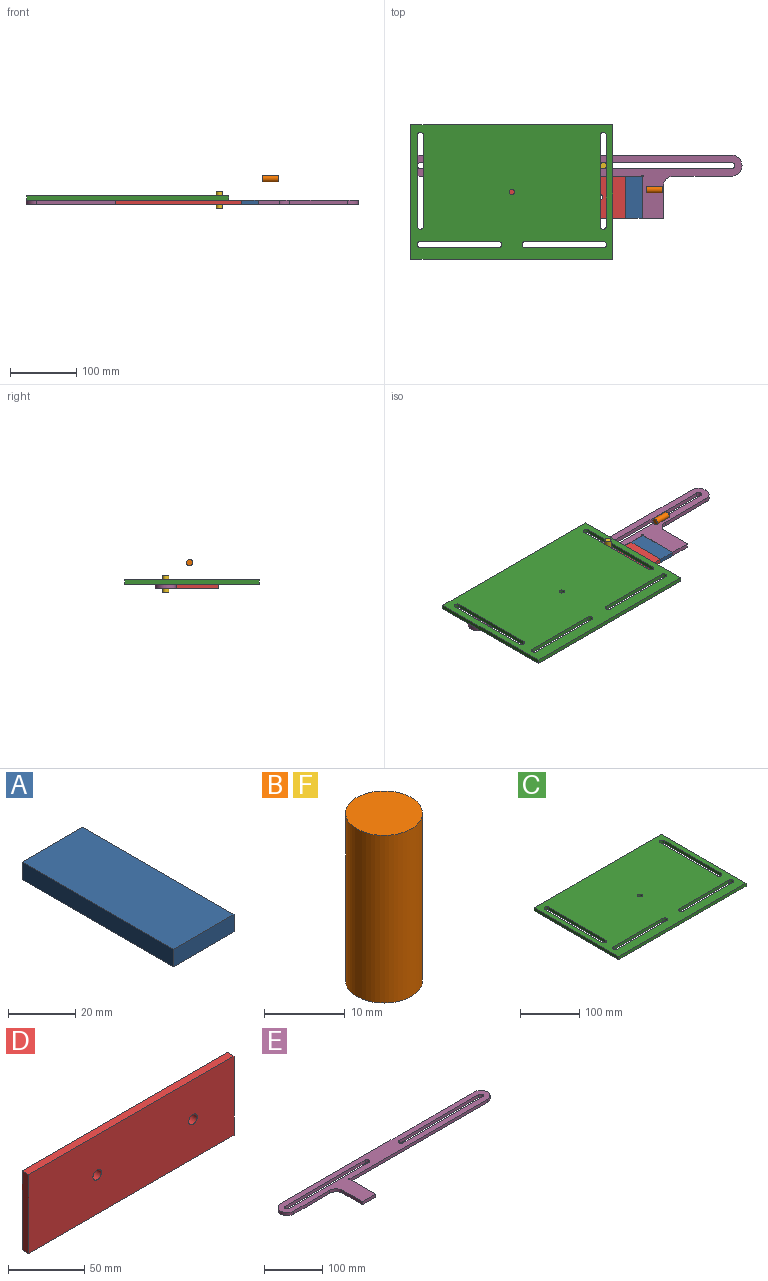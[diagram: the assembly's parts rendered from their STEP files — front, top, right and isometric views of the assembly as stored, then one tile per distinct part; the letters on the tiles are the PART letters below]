
ASSEMBLY  parts=6 mates=6
PART A: 6 faces, bbox 25.4x63.5x6.4 mm
  f0: plane 25.4x6.35mm, normal (0,1,0), area 161.3mm2, adj f1,f3,f4,f5
  f1: plane 63.5x6.35mm, normal (-1,0,0), area 403.2mm2, adj f0,f2,f4,f5
  f2: plane 25.4x6.35mm, normal (0,-1,0), area 161.3mm2, adj f1,f3,f4,f5
  f3: plane 63.5x6.35mm, normal (1,0,0), area 403.2mm2, adj f0,f2,f4,f5
  f4: plane 63.5x25.4mm, normal (0,0,1), area 1612.9mm2, adj f0,f1,f2,f3
  f5: plane 63.5x25.4mm, normal (0,0,-1), area 1612.9mm2, adj f0,f1,f2,f3
PART B: 3 faces, bbox 9.5x9.5x25.4 mm
  f0: cylinder r=4.76mm len=25.4mm, axis (0,0,-1), area 760.1mm2, adj f1,f2
  f1: plane 9.53x9.53mm, normal (0,0,1), area 71.3mm2, adj f0
  f2: plane 9.53x9.53mm, normal (0,0,-1), area 71.3mm2, adj f0
PART C: 23 faces, bbox 304.8x203.2x6.4 mm
  f0: plane 304.8x6.35mm, normal (0,1,0), area 1935.5mm2, adj f1,f20,f21,f22
  f1: plane 203.2x6.35mm, normal (-1,0,0), area 1290.3mm2, adj f0,f2,f21,f22
  f2: plane 304.8x6.35mm, normal (0,-1,0), area 1935.5mm2, adj f1,f20,f21,f22
  f3: cylinder r=4.76mm len=9.53mm, axis (0,0,-1), area 95mm2, adj f4,f16,f21,f22
  f4: plane 136.8x6.35mm, normal (-1,0,0), area 868.7mm2, adj f3,f5,f21,f22
  f5: cylinder r=4.76mm len=9.53mm, axis (0,0,-1), area 95mm2, adj f4,f16,f21,f22
  f6: cylinder r=4.76mm len=9.53mm, axis (0,0,-1), area 95mm2, adj f7,f17,f21,f22
  f7: plane 117.95x6.35mm, normal (0,1,0), area 749mm2, adj f6,f8,f21,f22
  f8: cylinder r=4.76mm len=9.53mm, axis (0,0,-1), area 95mm2, adj f7,f17,f21,f22
  f9: cylinder r=4.76mm len=9.53mm, axis (0,0,-1), area 95mm2, adj f10,f18,f21,f22
  f10: plane 117.95x6.35mm, normal (0,-1,0), area 749mm2, adj f9,f11,f21,f22
  f11: cylinder r=4.76mm len=9.53mm, axis (0,0,-1), area 95mm2, adj f10,f18,f21,f22
  f12: cylinder r=4.76mm len=9.53mm, axis (0,0,-1), area 95mm2, adj f13,f19,f21,f22
  f13: plane 136.8x6.35mm, normal (-1,0,0), area 868.7mm2, adj f12,f14,f21,f22
  f14: cylinder r=4.76mm len=9.53mm, axis (0,0,-1), area 95mm2, adj f13,f19,f21,f22
  f15: cylinder r=3.97mm len=7.94mm, axis (0,0,-1), area 158.3mm2, adj f21,f22
  f16: plane 136.8x6.35mm, normal (1,0,0), area 868.7mm2, adj f3,f5,f21,f22
  f17: plane 117.95x6.35mm, normal (0,-1,0), area 749mm2, adj f6,f8,f21,f22
  f18: plane 117.95x6.35mm, normal (0,1,0), area 749mm2, adj f9,f11,f21,f22
  f19: plane 136.8x6.35mm, normal (1,0,0), area 868.7mm2, adj f12,f14,f21,f22
  f20: plane 203.2x6.35mm, normal (1,0,0), area 1290.3mm2, adj f0,f2,f21,f22
  f21: plane 304.8x203.2mm, normal (0,0,1), area 56747.8mm2, adj f0,f1,f2,f3,f4,f5,f6,f7
  f22: plane 304.8x203.2mm, normal (0,0,-1), area 56747.8mm2, adj f0,f1,f2,f3,f4,f5,f6,f7
PART D: 8 faces, bbox 190.5x6.4x63.5 mm
  f0: plane 63.5x6.35mm, normal (-1,0,0), area 403.2mm2, adj f1,f3,f4,f5
  f1: plane 190.5x6.35mm, normal (0,0,-1), area 1209.7mm2, adj f0,f2,f4,f5
  f2: plane 63.5x6.35mm, normal (1,0,0), area 403.2mm2, adj f1,f3,f4,f5
  f3: plane 190.5x6.35mm, normal (0,0,1), area 1209.7mm2, adj f0,f2,f4,f5
  f4: plane 190.5x63.5mm, normal (0,-1,0), area 11997.8mm2, adj f0,f1,f2,f3,f6,f7
  f5: plane 190.5x63.5mm, normal (0,1,0), area 11997.8mm2, adj f0,f1,f2,f3,f6,f7
  f6: cylinder r=3.97mm len=7.94mm, axis (0,-1,0), area 158.3mm2, adj f4,f5
  f7: cylinder r=3.97mm len=7.94mm, axis (0,-1,0), area 158.3mm2, adj f4,f5
PART E: 20 faces, bbox 501.7x95.3x6.4 mm
  f0: cylinder r=4.76mm len=9.53mm, axis (0,0,-1), area 95mm2, adj f1,f17,f18,f19
  f1: plane 193.68x6.35mm, normal (0,-1,0), area 1229.8mm2, adj f0,f2,f18,f19
  f2: cylinder r=4.76mm len=9.53mm, axis (0,0,-1), area 95mm2, adj f1,f17,f18,f19
  f3: plane 31.75x6.35mm, normal (0,-1,0), area 201.6mm2, adj f4,f15,f18,f19
  f4: plane 61.9x6.35mm, normal (1,0,0), area 393.1mm2, adj f3,f5,f18,f19
  f5: cylinder r=1.6mm len=6.35mm, axis (0,0,-1), area 47.9mm2, adj f4,f6,f18,f19
  f6: plane 333.38x6.35mm, normal (0,-1,0), area 2116.9mm2, adj f5,f7,f18,f19
  f7: cylinder r=15.88mm len=31.75mm, axis (0,0,-1), area 316.7mm2, adj f6,f8,f18,f19
  f8: plane 469.9x6.35mm, normal (0,1,0), area 2983.9mm2, adj f7,f9,f18,f19
  f9: cylinder r=15.88mm len=31.75mm, axis (0,0,-1), area 316.7mm2, adj f8,f10,f18,f19
  f10: plane 87.3x6.35mm, normal (0,-1,0), area 554.4mm2, adj f9,f11,f18,f19
  f11: cylinder r=15.88mm len=15.88mm, axis (0,0,-1), area 158.3mm2, adj f10,f15,f18,f19
  f12: plane 193.68x6.35mm, normal (0,-1,0), area 1229.8mm2, adj f13,f16,f18,f19
  f13: cylinder r=4.76mm len=9.53mm, axis (0,0,-1), area 95mm2, adj f12,f14,f18,f19
  f14: plane 193.68x6.35mm, normal (0,1,0), area 1229.8mm2, adj f13,f16,f18,f19
  f15: plane 47.63x6.35mm, normal (-1,0,0), area 302.4mm2, adj f3,f11,f18,f19
  f16: cylinder r=4.76mm len=9.53mm, axis (0,0,-1), area 95mm2, adj f12,f14,f18,f19
  f17: plane 193.68x6.35mm, normal (0,1,0), area 1229.8mm2, adj f0,f2,f18,f19
  f18: plane 501.65x95.25mm, normal (0,0,1), area 13943.2mm2, adj f0,f1,f2,f3,f4,f5,f6,f7
  f19: plane 501.65x95.25mm, normal (0,0,-1), area 13943.2mm2, adj f0,f1,f2,f3,f4,f5,f6,f7
PART F: same geometry as B
PLACE A t=(774.43,-37.01,-9.32)mm
PLACE B rot(axis=(-0.58,-0.58,0.58),120deg) t=(228.38,79.34,-117.23)mm
PLACE C t=(152.5,-101.41,-2.97)mm fixed
PLACE D rot(axis=(1,0,0),90deg) t=(108.78,-54.37,-2.97)mm
PLACE E rot(axis=(0,-1,0),180deg) t=(-55.33,81.24,3.38)mm
PLACE F rot(axis=(0,0,1),90deg) t=(-8.47,115.7,-15.67)mm
MATE parallel C.f2 <-> E.f6  axis (0,-1,0) through (0.1,-101.41,0.2)mm
MATE pin_slot F.f0 <-> E.f13  axis (0,0,-1) through (138.21,39.97,-2.97)mm
MATE planar C.f22 <-> D.f5  axis (0,0,-1) through (0.1,2.74,-2.97)mm
MATE fastened A.f5 <-> E.f5  axis (0,0,-1) through (197.1,24.09,-9.32)mm
MATE pin_slot F.f0 <-> C.f5  axis (0,0,-1) through (138.21,39.97,-2.97)mm
MATE fastened D.f4 <-> A.f5  axis (0,0,-1) through (171.7,24.09,-9.32)mm
